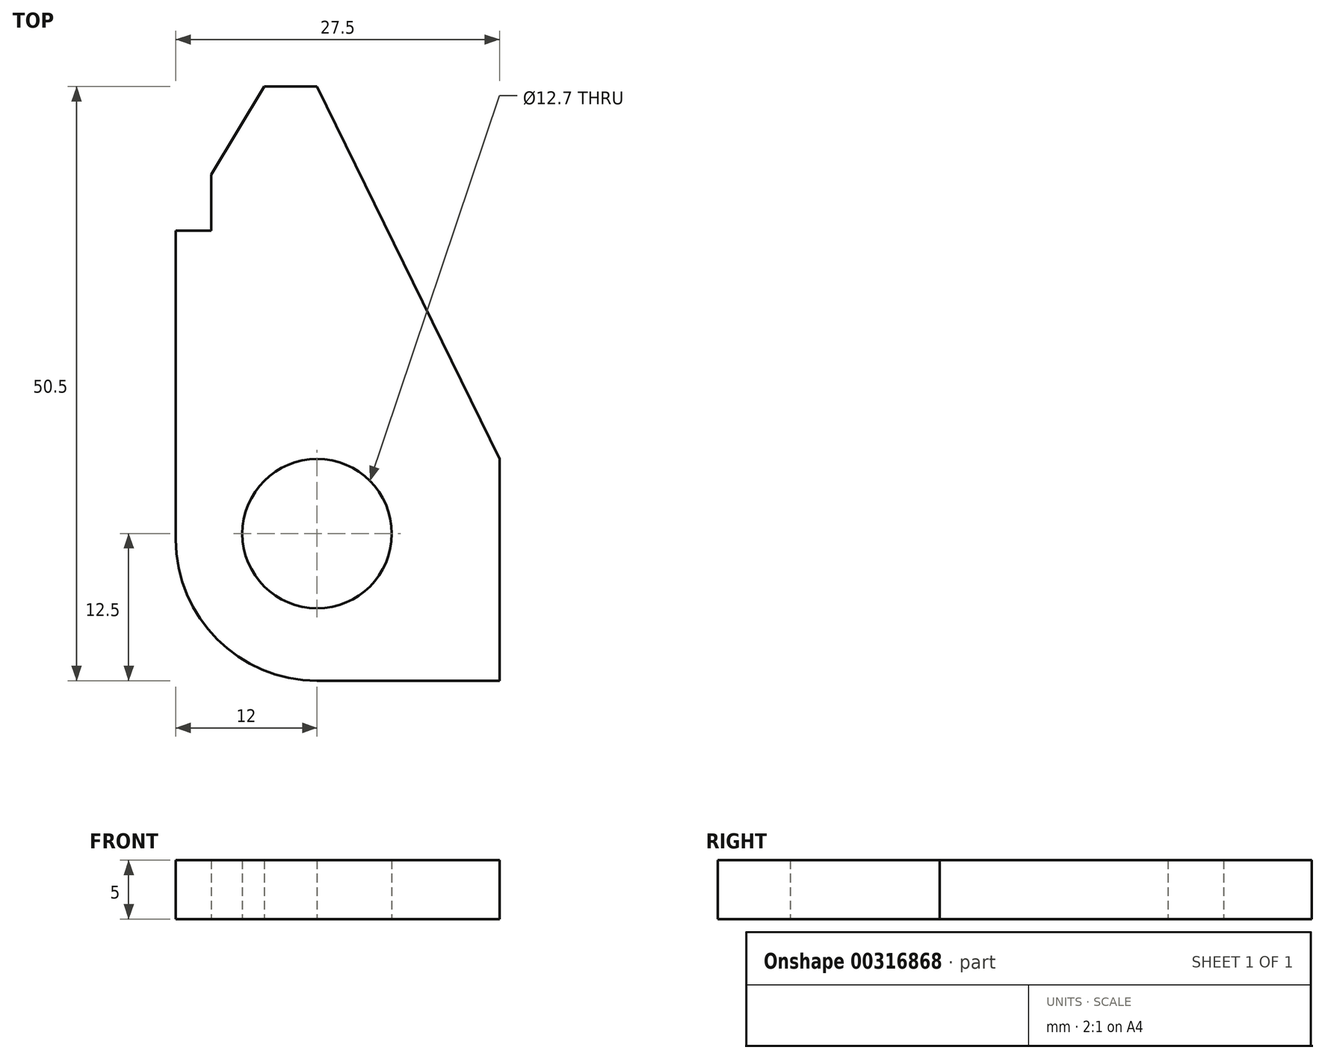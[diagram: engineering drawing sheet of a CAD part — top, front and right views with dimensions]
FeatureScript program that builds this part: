
annotation { "Feature Type Name" : "Feature", "Feature Type Description" : "" }
export const myFeature = defineFeature(function(context is Context, id is Id, definition is map)
    precondition{}
    {
        {
            var Q0;
            Q0=qCreatedBy(makeId("Top.planeOp"),FACE);
            var sketch = newSketch(context, id + "F0", { "sketchPlane" : qUnion([Q0])});
            skLineSegment(sketch, "E0.bottom", {"start": v(12, 0) * mm, "end": v(27.5, 0) * mm});
            skLineSegment(sketch, "E0.top", {"start": v(0, 50.5) * mm, "end": v(27.5, 50.5) * mm});
            skLineSegment(sketch, "E0.left", {"start": v(0, 12) * mm, "end": v(0, 50.5) * mm});
            skLineSegment(sketch, "E0.right", {"start": v(27.5, 0) * mm, "end": v(27.5, 50.5) * mm});
            skLineSegment(sketch, "E1", {"start": v(0, 0) * mm, "end": v(12, 12.5) * mm, "construction": true});
            skCircle(sketch, "E2", {"center": v(12, 12.5) * mm, "radius": 6.35 * mm});
            skLineSegment(sketch, "E3", {"start": v(27.5, 18.85) * mm, "end": v(12, 50.5) * mm});
            skLineSegment(sketch, "E4", {"start": v(12, 50.5) * mm, "end": v(7.5, 50.5) * mm});
            skLineSegment(sketch, "E5", {"start": v(0, 38.25) * mm, "end": v(3, 38.25) * mm});
            skLineSegment(sketch, "E6", {"start": v(3, 38.25) * mm, "end": v(3, 43) * mm});
            skLineSegment(sketch, "E7", {"start": v(3, 43) * mm, "end": v(7.5, 50.5) * mm});
            skPoint(sketch, "E8.visualSharp", {"position": v(0, 0) * mm});
            skArc(sketch, "E8.filletArc", {"start": v(0, 12) * mm, "mid": v(3.51, 3.51) * mm, "end": v(12, 0) * mm});
            skSolve(sketch);
        }
        {
            var Q0;
            {var subQ4=sQuery(id+"F0.wireOp",EDGE,"E0.bottom");Q0=makeQuery(id+"F0.imprint","IMPRINT",FACE,{"disambiguationData":[TD([[makeQuery(id+"F0.imprint","IMPRINT",EDGE,{"derivedFrom":subQ4}),1.0]])]});}
            extrude(context, id + "F1", {"entities" : qUnion([Q0]), "depth" : 5 * mm});
        }
    });
